# Revit family: ledflood-p_re440-125w-4000-as-bl_140062033
name_source: partatom
category: Leuchten
revit_build: Autodesk Revit 2016 (Build: 20190508_0715(x64)
units: mm (PartAtom-declared; Revit-internal decimal feet)

## family parameters
Basisbauteil = Fläche
Beim Laden mit Abzugskörper schneiden = Nein
Bemaßung runder Anschluss = Durchmesser verwenden
Gemeinsam genutzt = Nein
Lichtquelle = Nein
Raumberechnungspunkt = Nein
Teiletyp = Normal

## types (1)
- LEDFlood-P Re440-125W-4000-AS-BL (1 x LED, 15625 lm)
    Approval mark = CE, ENEC
    Beschreibung = Precise optical design for area-, object- and façade lighting. Super slim aluminium body with integrated heatsink and clipless cover. High energy saving up to 65% compared to halogen and high pressure sodium lamps. Robust design with high protection against water and dust. Equipped with a valve to regulate pressure differences.
    CIE Flux Codes = 63 93 99 100 100
    Control Gear = Electronic ballast
    Height = 65 mm
    Hersteller = OPPLE
    Lamp Light Flux = 15625 lm
    Lamp count = 1
    Lampe = 1 x LED
    Length = 440 mm
    Luminous efficacy = 125 lm/W
    ModVariant = Nein
    Modell = 140062033
    Mounting Place = Wall
    Mounting Type = Surface mounted
    Number of Poles = 1
    OnlyDefault = Ja
    Power Factor = 1
    Product Name = LEDFlood-P Re440-125W-4000-AS-BL
    Product group = Floodlight Performer
    ProductGroupID = 2005
    Protection Class = Protection class I
    Protection Degree = IP 66
    RLX_Detail_Level = 1
    RlxData = <blob elided: 48365 chars, md5=bea5bc62>
    Scheinlast = 125 VA
    Socket = socket
    Standby Power = 0 W
    System Light Flux = 15624 lm
    System Power = 125 W
    Typenbild = 140062033.jpg
    Typenkommentare = Product without accessories
    URL = http://relux.com
    VarID = ---
    Voltage = 0 V
    Vorgabe-Ansicht = 1800 mm
    Weight = 0.00 kg
    Width = 330 mm

## geometry (parser evidence)
native form markers: Blend x4, Sweep x9
no freeform markers — native parametric forms only
